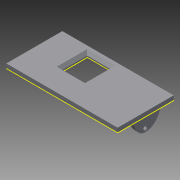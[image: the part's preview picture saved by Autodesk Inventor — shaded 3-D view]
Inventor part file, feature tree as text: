
AUTODESK INVENTOR PART (.ipt)
format: ipt  version: 2014 (Build 180170000, 170)  size: 171,008 bytes
history: native  units: mm
features: sketch x9, extrude x7, reference x7, chamfer x2, projected_geometry x1
ambient origin geometry x8: Origin, YZ Plane, XZ Plane, XY Plane, X Axis, Y Axis, Z Axis, Center Point
bodies: Solid1 (feature_tree)
feature tree (26):
  extrude  "Extrusion1"  Depth=16.0mm
  extrude  "Extrusion2"  Depth=18.0mm
  chamfer  "Chamfer1"  Distance=3.0mm
  extrude  "Extrusion3"  Depth=3.0mm TaperAngle=0.0deg
  extrude  "Extrusion4"  Depth=78.5mm
  sketch  "Sketch5"  dims[d14=78.5mm d15=39.5mm]
  extrude  "Extrusion5"  Depth=3.0mm TaperAngle=0.0deg
  extrude  "Extrusion6"  Depth=2.4mm
  extrude  "Extrusion7"  Depth=10.0mm TaperAngle=0.0deg
  chamfer  "Chamfer2"  Distance=0.5mm Angle=45.0deg
  sketch  "Sketch9"
  sketch  "Sketch1"  dims[d0=3.0mm d1=0.0mm d2=16.0mm]
  reference  "Reference1"
  reference  "Reference2"
  sketch  "Sketch2"  dims[d3=17.5mm d4=18.0mm]
  reference  "Reference3"
  reference  "Reference4"
  reference  "Reference5"
  reference  "Reference6"
  sketch  "Sketch3"  dims[d6=41.0mm d7=3.0mm d8=0.0mm]
  reference  "Reference7"
  sketch  "Sketch4"  dims[d9=2.0mm d10=2.0mm d11=45.0deg d12=3.0mm d13=0.0mm]
  sketch  "Sketch6"  dims[d16=3.0mm d17=0.0mm d18=3.0mm d19=0.0mm]
  sketch  "Sketch7"  dims[d20=3.0mm d21=0.0mm d22=2.4mm]
  projected_geometry  "Projected Loop1"
  sketch  "Sketch8"  dims[d23=10.0mm d24=3.0mm d25=0.0mm d26=0.5mm d27=2.0mm d28=45.0deg]
